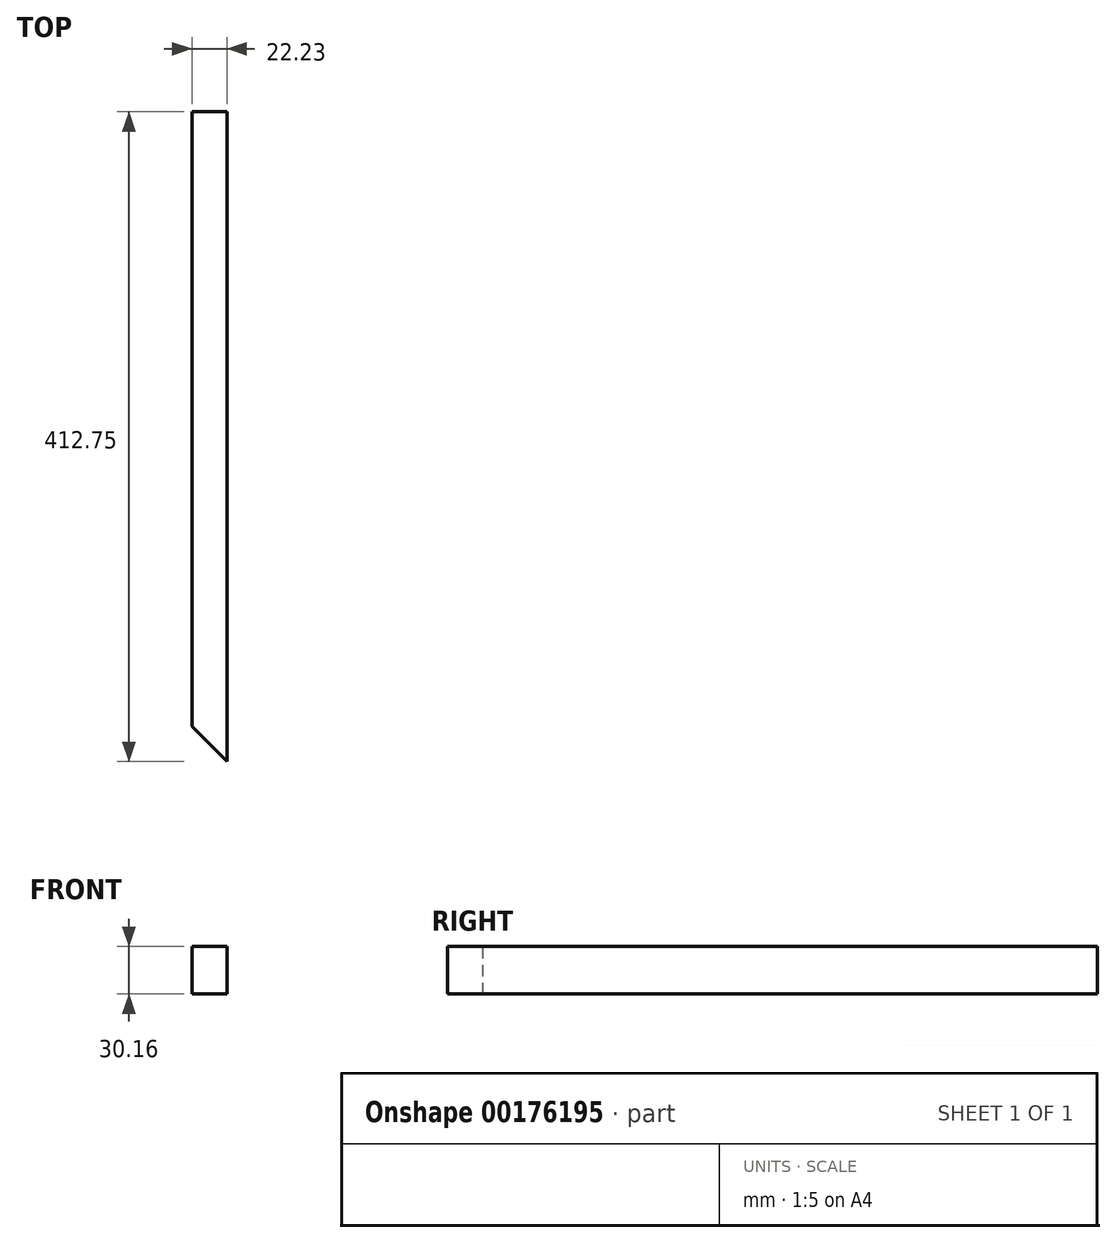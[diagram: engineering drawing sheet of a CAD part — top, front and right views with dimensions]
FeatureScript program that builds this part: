
annotation { "Feature Type Name" : "Feature", "Feature Type Description" : "" }
export const myFeature = defineFeature(function(context is Context, id is Id, definition is map)
    precondition{}
    {
        {
            var Q0;
            Q0=qCreatedBy(makeId("Top.planeOp"),FACE);
            var sketch = newSketch(context, id + "F0", { "sketchPlane" : qUnion([Q0])});
            skLineSegment(sketch, "E0", {"start": v(0, 22.22) * mm, "end": v(0, 412.75) * mm});
            skLineSegment(sketch, "E1", {"start": v(0, 412.75) * mm, "end": v(22.22, 412.75) * mm});
            skLineSegment(sketch, "E2", {"start": v(22.22, 412.75) * mm, "end": v(22.23, 0) * mm});
            skLineSegment(sketch, "E3", {"start": v(22.23, 0) * mm, "end": v(0, 22.22) * mm});
            skSolve(sketch);
        }
        {
            var Q0;
            Q0=makeQuery(id+"F0.imprint","IMPRINT",FACE,{"disambiguationData":[TD([[makeQuery(id+"F0.imprint","IMPRINT",EDGE,{"derivedFrom":sQuery(id+"F0.wireOp",EDGE,"E0")}),-1.0]])]});
            extrude(context, id + "F1", {"entities" : qUnion([Q0]), "depth" : 30.16 * mm});
        }
    });
